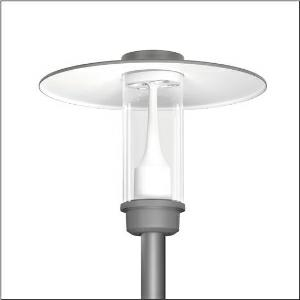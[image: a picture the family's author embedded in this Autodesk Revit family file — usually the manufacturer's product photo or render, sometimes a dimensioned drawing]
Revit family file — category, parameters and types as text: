
# Revit family: litepole_2_iq___st1_2a_5xa5425kf14h_4f30
name_source: partatom
category: Lighting Fixtures
units: mm (PartAtom-declared; Revit-internal decimal feet)

## family parameters
Cut with Voids When Loaded = No
Host = Face
Light Source = No
Part Type = Normal
Room Calculation Point = No
Round Connector Dimension = Use Diameter
Shared = No

## types (1)
- --- (1 x LED, 1550 lm, 10 W, 4000K)
    Apparent Load = 10 VA
    CIE Flux Codes = 22 60 92 98 100
    Color Rendering = 70
    Color Temperature = 4000K
    Default Elevation = 1800 mm
    Description = Litepole 2 iQ, mast luminaire, Module 540 iQ-SR, primary light control with 3 zone facetted reflector, of plastic, silver coated, highly specular, structured, primary optical cover: cover, of PMMA, transparent, light distribution: ST1.2a, light emission: direct distribution, primary light characteristic: asymmetric, installation type: post-top, LED, High Power LED, rated luminous flux: 1.550lm, luminous efficacy: 155lm/W, light colour: 740, colour temperature: 4000K, control gear: iQ Street-Remote, control: pre-setting: logarithmic dimming characteristic, Street-Remote, Auto-Match, Temp-Guard, Lumen-Switch, Night-Set, Smart-Wire, Light-Fading, Desk-Remote (wireless, voltage-free reading and setting of iQ features in the workshop via application-optimized NFC function/RFID function), optimised constant luminous flux control (CLO 2.0), with terminal, 6-pole, max. 2.5mm², mains connection: 230..240V, AC, 50/60Hz, start of lifetime: 10W, end of service life: 10W, reduction: 5W, luminaire housing, upper part, of aluminium, coated, Siteco® metallic grey (DB 702S), diameter: 750mm, height: 590mm, spigot size: d x l = 76 x 70mm (post-top) | with reducer (optional accessory) 60 x 70mm, mounting height: 3..5m, post-top mast mounting element, of diecast aluminium, coated, Siteco® metallic grey (DB 702S), Module 540 iQ-SR, traffic white (RAL 9016), equipment: standard, protection rating (complete): IP65, insulation class (complete): insulation class II (safety insulation), certification: CE, ENEC, VDE, packaging unit: 1 piece

Light Distribution: ST1.2a
    Height = 590 mm
    Lamp = 1 x LED
    Lamp Light Flux = 1550 lm
    Lamp Power = 10 W
    Lamp count = 1
    Length = 750 mm
    Luminous efficacy = 155 lm/W
    Manufacturer = Siteco
    ModVariant = No
    Model = 5XA5425KF14H
    Number of Poles = 1
    OnlyDefault = Yes
    Power Factor = 1
    Product Name = Litepole 2 iQ | ST1.2a
    Product group = mast luminaire | pylon top
    ProductGroupID = 6100
    Protection Class = Protection class II
    Protection Degree = IP 65
    RLX_Detail_Level = 1
    RLX_Emergency_Light_Flux = 0 lm
    RLX_Emergency_Type = 0
    RLX_Emergency_Type_DB = No
    RlxData = <blob elided: 67901 chars, md5=8dc1a5bd>
    Socket = socket
    Standby Power = 0 W
    System Light Flux = 1550 lm
    System Power = 10 W
    Type Comments = factory setting: luminous flux: 100 % | dim-lin: 254 | 401 mA
    Type Image = l_1006518.jpg
    URL = http://relux.com
    VarID = @adj_190075
    Voltage = 0 V
    Weight = 0.00 kg
    Width = 0 mm  [stored 0 ft]

note: [stored X ft] marks values corroborated as IEEE doubles in the binary element streams (Revit-internal decimal feet)

## geometry (parser evidence)
native form markers: Blend x4, Sweep x11
no freeform markers — native parametric forms only
